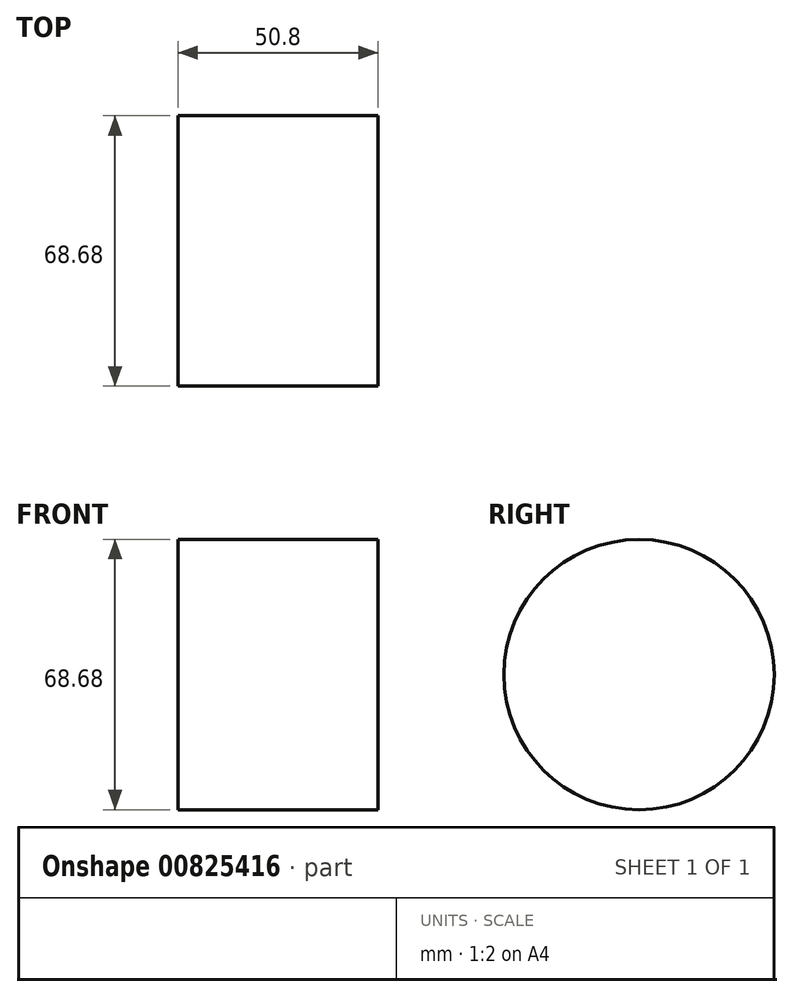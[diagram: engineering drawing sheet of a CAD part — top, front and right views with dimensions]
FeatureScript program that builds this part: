
annotation { "Feature Type Name" : "Feature", "Feature Type Description" : "" }
export const myFeature = defineFeature(function(context is Context, id is Id, definition is map)
    precondition{}
    {
        {
            var Q0;
            Q0=qCreatedBy(makeId("Right.planeOp"),FACE);
            var sketch = newSketch(context, id + "F0", { "sketchPlane" : qUnion([Q0])});
            skCircle(sketch, "E0", {"center": v(0, 0) * mm, "radius": 34.34 * mm});
            skSolve(sketch);
        }
        {
            var Q0;
            Q0=makeQuery(id+"F0.imprint","IMPRINT",FACE,{"disambiguationData":[TD([[makeQuery(id+"F0.imprint","IMPRINT",EDGE,{"derivedFrom":sQuery(id+"F0.wireOp",EDGE,"E0")}),1.0]])]});
            extrude(context, id + "F1", {"entities" : qUnion([Q0]), "depth" : 25.4 * mm, "offsetDistance" : 25.4 * mm});
        }
        {
            var Q0;
            Q0=makeQuery(id+"F1.opExtrude","SWEPT_BODY",BODY,{"disambiguationData":[OSD([sQuery(id+"F0.wireOp",EDGE,"E0")])]});
            var Q1;
            Q1=qCreatedBy(makeId("Right.planeOp"),FACE);
            mirror(context, id + "F2", {"operationType" : NewBodyOperationType.ADD, "entities" : qUnion([Q0]), "mirrorPlane" : qUnion([Q1])});
        }
    });
